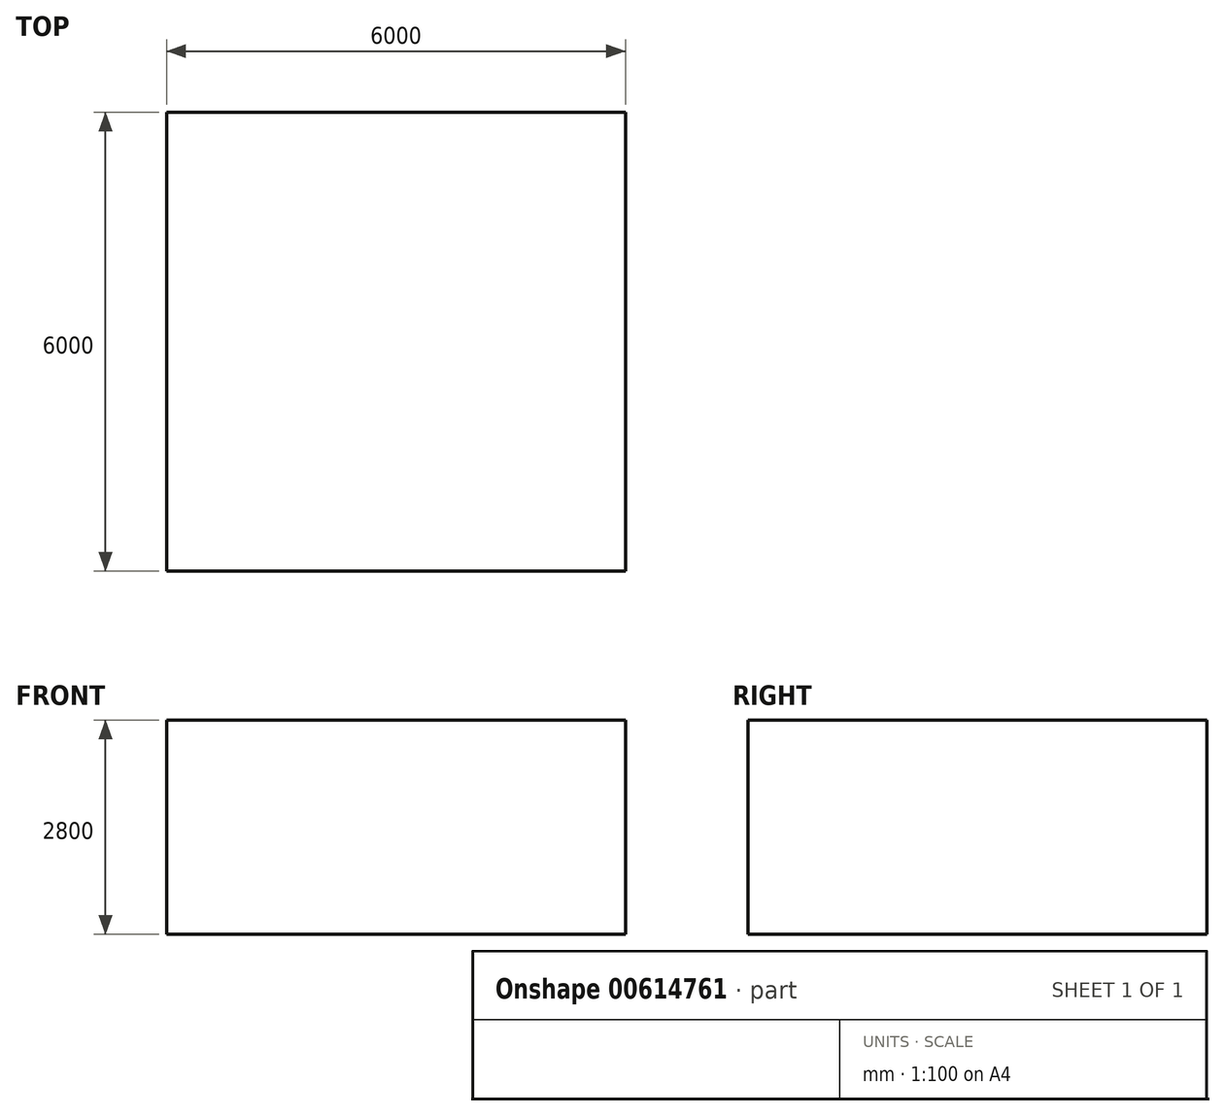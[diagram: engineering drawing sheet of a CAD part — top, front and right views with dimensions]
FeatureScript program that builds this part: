
annotation { "Feature Type Name" : "Feature", "Feature Type Description" : "" }
export const myFeature = defineFeature(function(context is Context, id is Id, definition is map)
    precondition{}
    {
        {
            var Q0;
            Q0=qCreatedBy(makeId("Top.planeOp"),FACE);
            var sketch = newSketch(context, id + "F0", { "sketchPlane" : qUnion([Q0])});
            skLineSegment(sketch, "E0.bottom", {"start": v(0, 0) * mm, "end": v(6000, 0) * mm});
            skLineSegment(sketch, "E0.top", {"start": v(0, 6000) * mm, "end": v(6000, 6000) * mm});
            skLineSegment(sketch, "E0.left", {"start": v(0, 0) * mm, "end": v(0, 6000) * mm});
            skLineSegment(sketch, "E0.right", {"start": v(6000, 0) * mm, "end": v(6000, 6000) * mm});
            skSolve(sketch);
        }
        {
            var Q0;
            Q0=makeQuery(id+"F0.imprint","IMPRINT",FACE,{"disambiguationData":[TD([[makeQuery(id+"F0.imprint","IMPRINT",EDGE,{"derivedFrom":sQuery(id+"F0.wireOp",EDGE,"E0.bottom")}),1.0]])]});
            extrude(context, id + "F1", {"entities" : qUnion([Q0]), "depth" : 2800 * mm, "offsetDistance" : 25 * mm});
        }
    });
